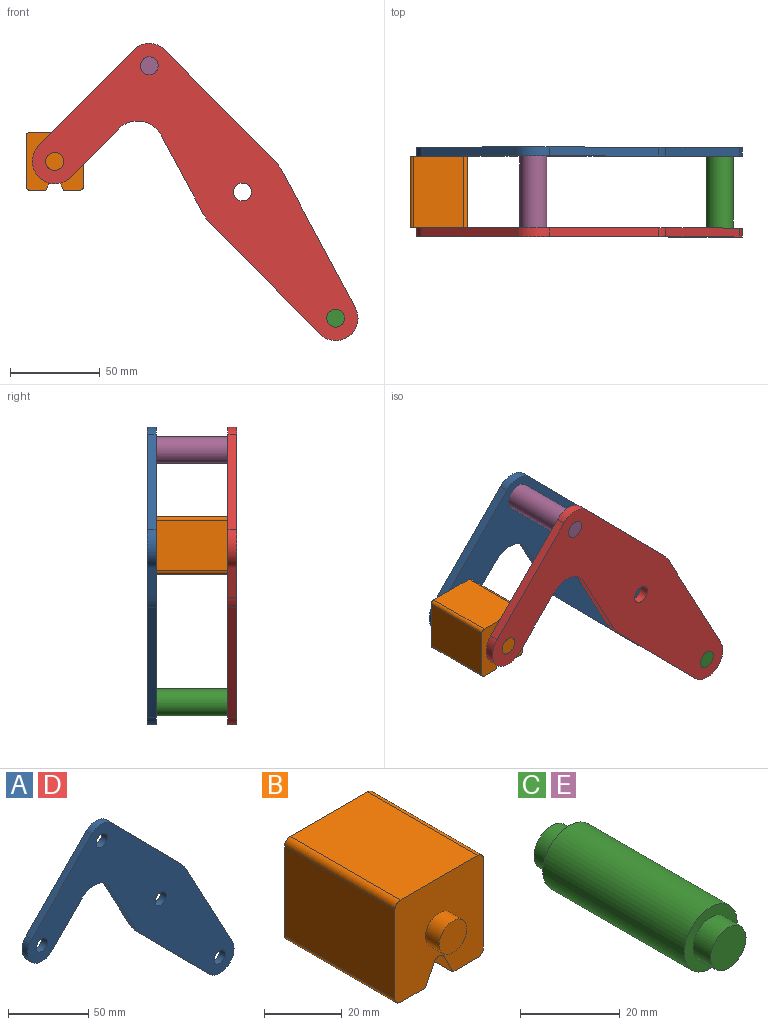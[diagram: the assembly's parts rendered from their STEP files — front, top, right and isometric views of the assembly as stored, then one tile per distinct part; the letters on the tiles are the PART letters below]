
ASSEMBLY  parts=5 mates=3
PART A: 18 faces, bbox 181.7x5x165.8 mm
  f0: plane 43.49x23.35mm, normal (-0.88,0,-0.47), area 246.8mm2, adj f1,f14,f16,f17
  f1: cylinder r=25mm len=5.75mm, axis (0,1,0), area 35.8mm2, adj f0,f2,f16,f17
  f2: plane 61.6x60.87mm, normal (-0.71,0,-0.7), area 433mm2, adj f1,f3,f16,f17
  f3: cylinder r=12.5mm len=21.39mm, axis (0,1,0), area 178.4mm2, adj f2,f4,f16,f17
  f4: plane 76.3x40.96mm, normal (0.88,0,0.47), area 433mm2, adj f3,f5,f16,f17
  f5: cylinder r=25mm len=5.75mm, axis (0,1,0), area 35.8mm2, adj f4,f6,f16,f17
  f6: plane 61.6x60.87mm, normal (0.71,0,0.7), area 433mm2, adj f5,f7,f16,f17
  f7: cylinder r=12.5mm len=17.78mm, axis (0,1,0), area 98.9mm2, adj f6,f8,f16,f17
  f8: plane 53.35x52.71mm, normal (-0.71,0,0.7), area 375mm2, adj f7,f9,f16,f17
  f9: cylinder r=12.5mm len=21.39mm, axis (0,1,0), area 196.3mm2, adj f8,f10,f16,f17
  f10: plane 26.86x26.54mm, normal (0.71,0,-0.7), area 188.8mm2, adj f9,f14,f16,f17
  f11: cylinder r=5mm len=10mm, axis (0,1,0), area 157.1mm2, adj f16,f17
  f12: cylinder r=5mm len=10mm, axis (0,1,0), area 157.1mm2, adj f16,f17
  f13: cylinder r=5mm len=10mm, axis (0,1,0), area 157.1mm2, adj f16,f17
  f14: cylinder r=15mm len=23.89mm, axis (0,1,0), area 140.2mm2, adj f0,f10,f16,f17
  f15: cylinder r=5mm len=10mm, axis (0,1,0), area 157.1mm2, adj f16,f17
  f16: plane 181.66x165.78mm, normal (0,-1,0), area 8710.1mm2, adj f0,f1,f2,f3,f4,f5,f6,f7
  f17: plane 181.66x165.78mm, normal (0,1,0), area 8710.1mm2, adj f0,f1,f2,f3,f4,f5,f6,f7
PART B: 18 faces, bbox 32.1x50x32.1 mm
  f0: plane 40x28.08mm, normal (1,0,0), area 1123.1mm2, adj f4,f10,f13,f14
  f1: plane 40x9.04mm, normal (0,0,-1), area 361.6mm2, adj f2,f4,f10,f14
  f2: plane 40x6.42mm, normal (-0.89,0,-0.45), area 287.2mm2, adj f1,f4,f10,f15
  f3: plane 40x6.42mm, normal (0.89,0,-0.45), area 287.2mm2, adj f4,f5,f10,f15
  f4: plane 32.08x32.08mm, normal (0,-1,0), area 900.6mm2, adj f0,f1,f2,f3,f5,f6,f7,f9
  f5: plane 40x9.04mm, normal (0,0,-1), area 361.6mm2, adj f3,f4,f10,f16
  f6: plane 40x28.08mm, normal (0,0,1), area 1123.1mm2, adj f4,f10,f13,f17
  f7: plane 40x28.08mm, normal (-1,0,0), area 1123.1mm2, adj f4,f10,f16,f17
  f8: plane 10x10mm, normal (0,-1,0), area 78.5mm2, adj f9
  f9: cylinder r=5mm len=10mm, axis (0,1,0), area 157.1mm2, adj f4,f8
  f10: plane 32.08x32.08mm, normal (0,1,0), area 900.6mm2, adj f0,f1,f2,f3,f5,f6,f7,f12
  f11: plane 10x10mm, normal (0,1,0), area 78.5mm2, adj f12
  f12: cylinder r=5mm len=10mm, axis (0,-1,0), area 157.1mm2, adj f10,f11
  f13: cylinder r=2mm len=40mm, axis (0,1,0), area 125.7mm2, adj f0,f4,f6,f10
  f14: cylinder r=2mm len=40mm, axis (0,-1,0), area 125.7mm2, adj f0,f1,f4,f10
  f15: cylinder r=2mm len=40mm, axis (0,1,0), area 177.1mm2, adj f2,f3,f4,f10
  f16: cylinder r=2mm len=40mm, axis (0,1,0), area 125.7mm2, adj f4,f5,f7,f10
  f17: cylinder r=2mm len=40mm, axis (0,-1,0), area 125.7mm2, adj f4,f6,f7,f10
PART C: 7 faces, bbox 15x50x15 mm
  f0: cylinder r=7.5mm len=40mm, axis (0,-1,0), area 1885mm2, adj f2,f5
  f1: cylinder r=5mm len=10mm, axis (0,1,0), area 157.1mm2, adj f2,f3
  f2: plane 15x15mm, normal (0,-1,0), area 98.2mm2, adj f0,f1
  f3: plane 10x10mm, normal (0,-1,0), area 78.5mm2, adj f1
  f4: cylinder r=5mm len=10mm, axis (0,-1,0), area 157.1mm2, adj f5,f6
  f5: plane 15x15mm, normal (0,1,0), area 98.2mm2, adj f0,f4
  f6: plane 10x10mm, normal (0,1,0), area 78.5mm2, adj f4
PART D: same geometry as A
PART E: same geometry as C
PLACE A t=(0,25,0)mm
PLACE B t=(0,-20,0)mm
PLACE C t=(103.95,-20,-140.78)mm
PLACE D t=(0,-20,0)mm fixed
PLACE E t=(0,-20,0)mm
MATE revolute C.f0 <-> D.f3  axis (0,-1,0) through (51.98,-20,-70.39)mm
MATE revolute B.f9 <-> D.f9  axis (0,-1,0) through (-104.69,-20,17.04)mm
MATE revolute A.f7 <-> E.f0  axis (0,-1,0) through (-51.98,20,70.39)mm
